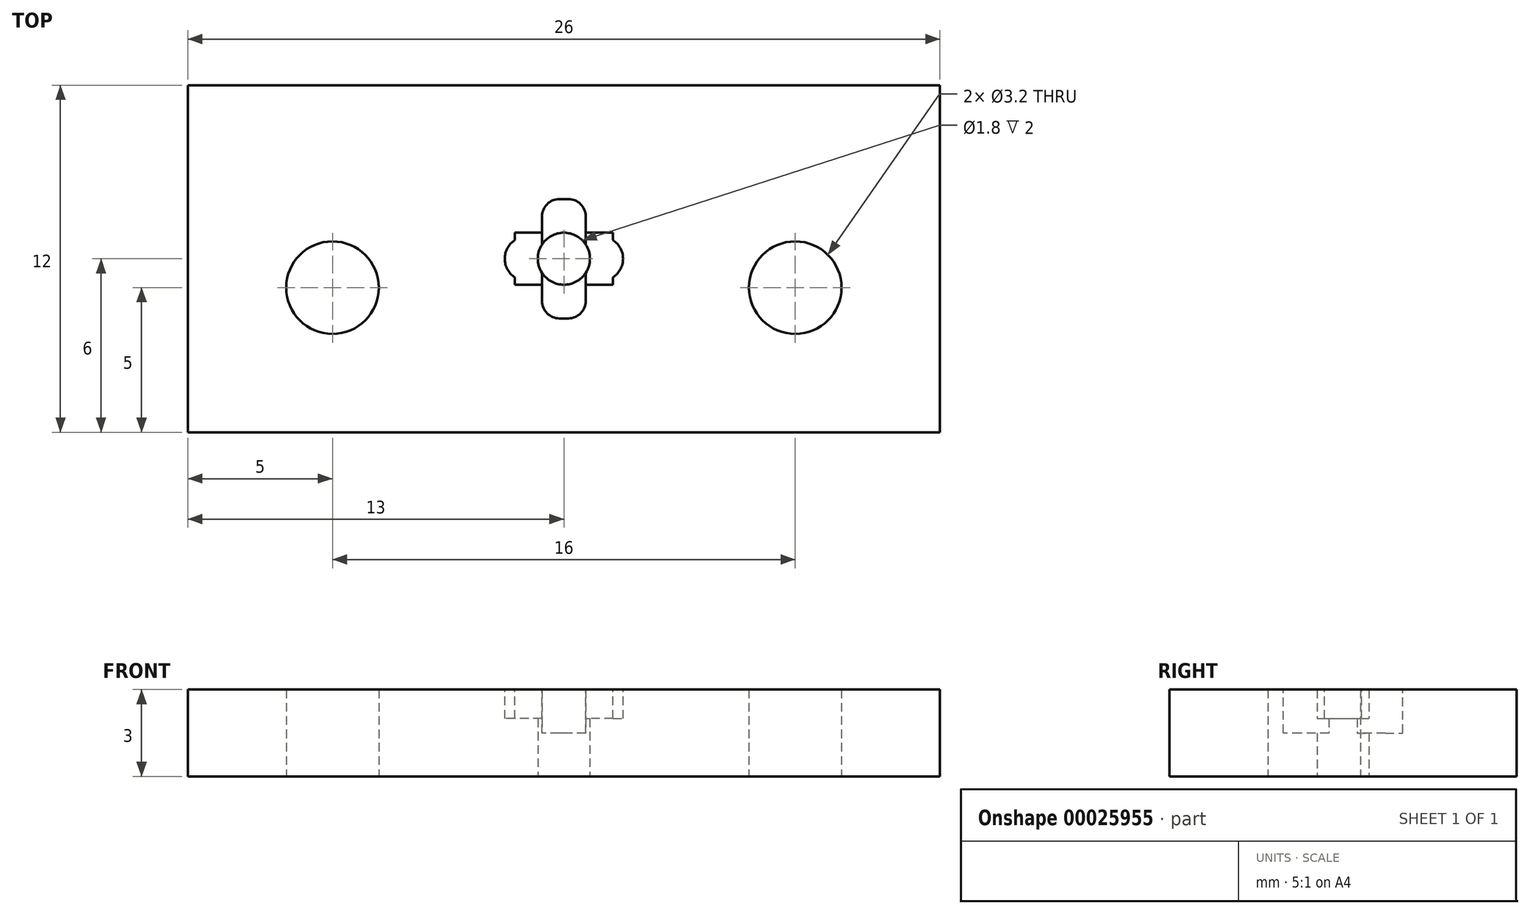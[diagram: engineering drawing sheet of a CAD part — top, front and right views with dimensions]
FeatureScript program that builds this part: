
annotation { "Feature Type Name" : "Feature", "Feature Type Description" : "" }
export const myFeature = defineFeature(function(context is Context, id is Id, definition is map)
    precondition{}
    {
        {
            var Q0;
            Q0=qCreatedBy(makeId("Top.planeOp"),FACE);
            var sketch = newSketch(context, id + "F0", { "sketchPlane" : qUnion([Q0])});
            skLineSegment(sketch, "E0.rect.bottom", {"start": v(13, -6) * mm, "end": v(-13, -6) * mm});
            skLineSegment(sketch, "E0.rect.top", {"start": v(13, 6) * mm, "end": v(-13, 6) * mm});
            skLineSegment(sketch, "E0.rect.left", {"start": v(13, -6) * mm, "end": v(13, 6) * mm});
            skLineSegment(sketch, "E0.rect.right", {"start": v(-13, -6) * mm, "end": v(-13, 6) * mm});
            skPoint(sketch, "E0.rect.middle", {"position": v(0, 0) * mm});
            skCircle(sketch, "E1", {"center": v(0, 0) * mm, "radius": 0.9 * mm});
            skCircle(sketch, "E2", {"center": v(-8, -1) * mm, "radius": 1.6 * mm});
            skLineSegment(sketch, "E3", {"start": v(0, 6) * mm, "end": v(0, -6) * mm, "construction": true});
            skCircle(sketch, "E4.MirrorC", {"center": v(8, -1) * mm, "radius": 1.6 * mm});
            skSolve(sketch);
        }
        {
            var Q0;
            Q0=qSketchRegion(id+"F0",true);
            extrude(context, id + "F1", {"entities" : qUnion([Q0]), "depth" : 3 * mm});
        }
        {
            var Q0;
            Q0=makeQuery(id+"F1.opExtrude","CAP_FACE",FACE,{"disambiguationData":[OSD([sQuery(id+"F0.wireOp",EDGE,"E0.rect.bottom"),sQuery(id+"F0.wireOp",EDGE,"E0.rect.top"),sQuery(id+"F0.wireOp",EDGE,"E0.rect.left"),sQuery(id+"F0.wireOp",EDGE,"E0.rect.right"),sQuery(id+"F0.wireOp",EDGE,"E1"),sQuery(id+"F0.wireOp",EDGE,"E2"),sQuery(id+"F0.wireOp",EDGE,"E4.MirrorC")])],"isStart":false});
            var sketch = newSketch(context, id + "F2", { "sketchPlane" : qUnion([Q0])});
            skPoint(sketch, "E5.rect.middle", {"position": v(0, 0) * mm});
            skLineSegment(sketch, "E6.rect.bottom", {"start": v(0.15, 2.06) * mm, "end": v(-0.15, 2.06) * mm});
            skLineSegment(sketch, "E6.rect.top", {"start": v(0.15, -2.06) * mm, "end": v(-0.15, -2.06) * mm});
            skLineSegment(sketch, "E6.rect.left", {"start": v(0.75, 1.46) * mm, "end": v(0.75, -1.46) * mm});
            skLineSegment(sketch, "E6.rect.right", {"start": v(-0.75, 1.46) * mm, "end": v(-0.75, -1.46) * mm});
            skPoint(sketch, "E7.visualSharp", {"position": v(-0.75, 2.06) * mm});
            skArc(sketch, "E7.filletArc", {"start": v(-0.15, 2.06) * mm, "mid": v(-0.58, 1.89) * mm, "end": v(-0.75, 1.46) * mm});
            skPoint(sketch, "E8.visualSharp", {"position": v(0.75, 2.06) * mm});
            skArc(sketch, "E8.filletArc", {"start": v(0.75, 1.46) * mm, "mid": v(0.58, 1.89) * mm, "end": v(0.15, 2.06) * mm});
            skPoint(sketch, "E9.visualSharp", {"position": v(0.75, -2.06) * mm});
            skArc(sketch, "E9.filletArc", {"start": v(0.15, -2.06) * mm, "mid": v(0.58, -1.89) * mm, "end": v(0.75, -1.46) * mm});
            skPoint(sketch, "E10.visualSharp", {"position": v(-0.75, -2.06) * mm});
            skArc(sketch, "E10.filletArc", {"start": v(-0.75, -1.46) * mm, "mid": v(-0.58, -1.89) * mm, "end": v(-0.15, -2.06) * mm});
            skSolve(sketch);
        }
        {
            var Q0;
            Q0 = qSketchRegion(id + "F2", true);
            extrude(context, id + "F3", {"entities" : qUnion([Q0]), "operationType" : NewBodyOperationType.REMOVE, "oppositeDirection" : true, "depth" : 1.5 * mm});
        }
        {
            var Q0;
            Q0=makeQuery(id+"F1.opExtrude","CAP_FACE",FACE,{"disambiguationData":[OSD([sQuery(id+"F0.wireOp",EDGE,"E0.rect.bottom"),sQuery(id+"F0.wireOp",EDGE,"E0.rect.top"),sQuery(id+"F0.wireOp",EDGE,"E0.rect.left"),sQuery(id+"F0.wireOp",EDGE,"E0.rect.right"),sQuery(id+"F0.wireOp",EDGE,"E1"),sQuery(id+"F0.wireOp",EDGE,"E2"),sQuery(id+"F0.wireOp",EDGE,"E4.MirrorC")])],"isStart":false});
            var sketch = newSketch(context, id + "F4", { "sketchPlane" : qUnion([Q0])});
            skLineSegment(sketch, "E11.rect.bottom", {"start": v(1.7, -0.9) * mm, "end": v(-1.7, -0.9) * mm});
            skLineSegment(sketch, "E11.rect.top", {"start": v(1.7, 0.9) * mm, "end": v(-1.7, 0.9) * mm});
            skLineSegment(sketch, "E11.rect.left", {"start": v(1.7, -0.9) * mm, "end": v(1.7, -0.64) * mm});
            skLineSegment(sketch, "E11.rect.right", {"start": v(-1.7, -0.9) * mm, "end": v(-1.7, -0.64) * mm});
            skPoint(sketch, "E11.rect.middle", {"position": v(0, 0) * mm});
            skLineSegment(sketch, "E12", {"start": v(0, 0) * mm, "end": v(-1.7, 0) * mm, "construction": true});
            skLineSegment(sketch, "E13", {"start": v(0, 0) * mm, "end": v(0, 0.9) * mm, "construction": true});
            skArc(sketch, "E14", {"start": v(-1.7, 0.64) * mm, "mid": v(-2.04, 0) * mm, "end": v(-1.7, -0.64) * mm});
            skLineSegment(sketch, "E15.trimOffspring", {"start": v(-1.7, 0.64) * mm, "end": v(-1.7, 0.9) * mm});
            skArc(sketch, "E16.MirrorCS", {"start": v(1.7, 0.64) * mm, "mid": v(2.04, 0) * mm, "end": v(1.7, -0.64) * mm});
            skLineSegment(sketch, "E17.trimOffspring", {"start": v(1.7, 0.64) * mm, "end": v(1.7, 0.9) * mm});
            skSolve(sketch);
        }
        {
            var Q0;
            Q0 = qSketchRegion(id + "F4", true);
            extrude(context, id + "F5", {"entities" : qUnion([Q0]), "operationType" : NewBodyOperationType.REMOVE, "oppositeDirection" : true, "depth" : 1 * mm});
        }
    });
